# Revit family: Geräteeinsätze GES_Geräteeinsatz_GESR9_mit_Griffbügel
name_source: partatom
category: Generic Models
revit_build: Autodesk Revit 2015 (Build: 20140606_1530(x64)
units: mm (PartAtom-declared; Revit-internal decimal feet)

## types (3) — shared parameters
Bodenbelagdicke = 5 mm  [stored 0.0164042 ft]
Diameter dimesion = 304 mm  [stored 0.997375 ft]
Height = 60 mm  [stored 0.19685 ft]
Inner cut = 287 mm  [stored 0.941601 ft]
Inner cut 3 = 230 mm  [stored 0.754593 ft]
Inner cut2 = 208 mm
Manufacturer = OBO Bettermann
Outer Diameter Dimension = 324 mm  [stored 1.06299 ft]
Snur width = 111 mm
URL = http://www.obo-bettermann.com

## per-type parameters (varying)
| type | GTIN | Manufacturer Art. No. | Material |
| GESR9 U 7011 | 4012195104162 | 7405528 | Plastic RAL 7011 |
| GESR9 U 9011 | 4012195104209 | 7405532 | Plastic RAL 9011 |
| GESR9 U 1019 | 4012195104216 | 7405536 | Plastic RAL 1019 |

note: column(s) folded — value = type name in every type: Article Type

note: [stored X ft] marks values corroborated as IEEE doubles in the binary element streams (Revit-internal decimal feet)

## geometry (parser evidence)
native form markers: Sweep x2
no freeform markers — native parametric forms only
